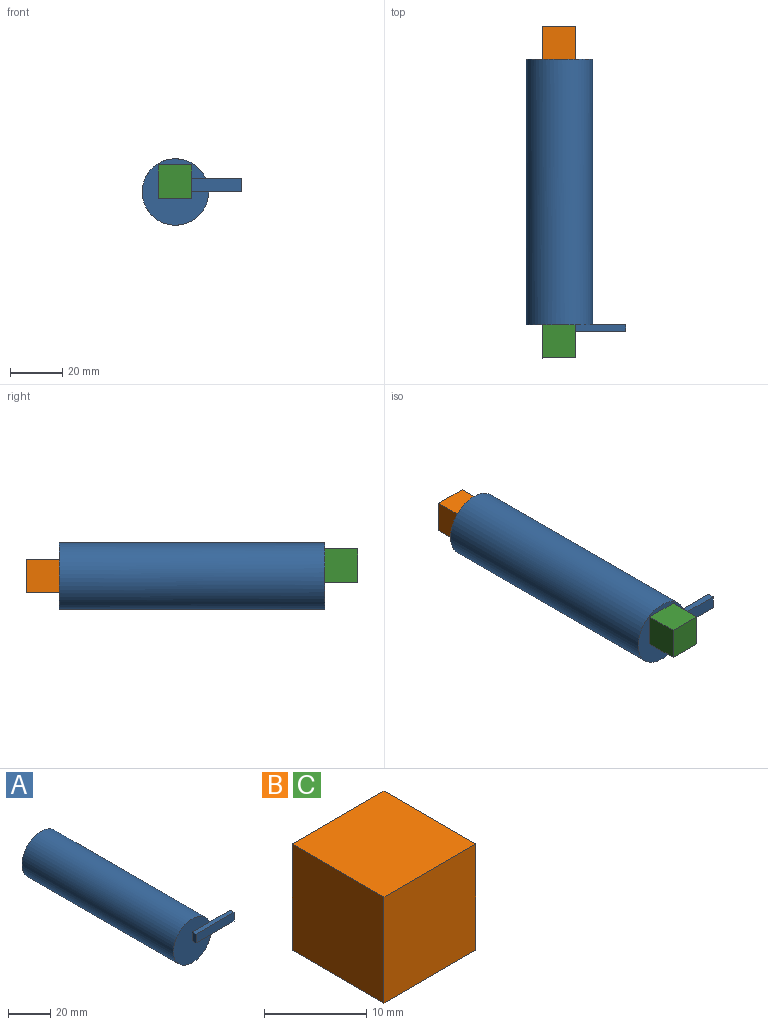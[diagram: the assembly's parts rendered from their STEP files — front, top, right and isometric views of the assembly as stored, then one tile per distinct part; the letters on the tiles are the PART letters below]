
ASSEMBLY  parts=3 mates=2
PART A: 9 faces, bbox 38.1x104.1x25.4 mm
  f0: plane 25.4x25.4mm, normal (0,-1,0), area 444mm2, adj f1,f4,f5,f6
  f1: cylinder r=12.7mm len=101.6mm, axis (0,1,0), area 8107.3mm2, adj f0,f2,f3
  f2: plane 25.4x25.4mm, normal (0,1,0), area 506.7mm2, adj f1
  f3: plane 13.76x5.08mm, normal (0,1,0), area 66.3mm2, adj f1,f4,f6,f7
  f4: plane 25.4x2.54mm, normal (0,0,1), area 64.5mm2, adj f0,f3,f5,f7,f8
  f5: plane 5.08x2.54mm, normal (-1,0,0), area 12.9mm2, adj f0,f4,f6,f8
  f6: plane 25.4x2.54mm, normal (0,0,-1), area 64.5mm2, adj f0,f3,f5,f7,f8
  f7: plane 5.08x2.54mm, normal (1,0,0), area 12.9mm2, adj f3,f4,f6,f8
  f8: plane 25.4x5.08mm, normal (0,-1,0), area 129mm2, adj f4,f5,f6,f7
PART B: 6 faces, bbox 12.7x12.7x12.7 mm
  f0: plane 12.7x12.7mm, normal (0,0,-1), area 161.3mm2, adj f1,f3,f4,f5
  f1: plane 12.7x12.7mm, normal (1,0,0), area 161.3mm2, adj f0,f2,f4,f5
  f2: plane 12.7x12.7mm, normal (0,0,1), area 161.3mm2, adj f1,f3,f4,f5
  f3: plane 12.7x12.7mm, normal (-1,0,0), area 161.3mm2, adj f0,f2,f4,f5
  f4: plane 12.7x12.7mm, normal (0,-1,0), area 161.3mm2, adj f0,f1,f2,f3
  f5: plane 12.7x12.7mm, normal (0,1,0), area 161.3mm2, adj f0,f1,f2,f3
PART C: same geometry as B
PLACE A rot(axis=(0,-1,0),0deg) t=(15.7,-16.86,-2.92)mm
PLACE B rot(axis=(0,-1,0),0deg) t=(15.7,-4.16,-31.49)mm
PLACE C rot(axis=(0,-1,0),0deg) t=(15.57,-118.46,-27.5)mm
MATE slider B.f4 <-> A.f1  axis (0,-1,0) through (15.7,-16.86,-2.92)mm
MATE planar C.f5 <-> A.f0  axis (0,1,0) through (15.57,-118.46,1.07)mm
